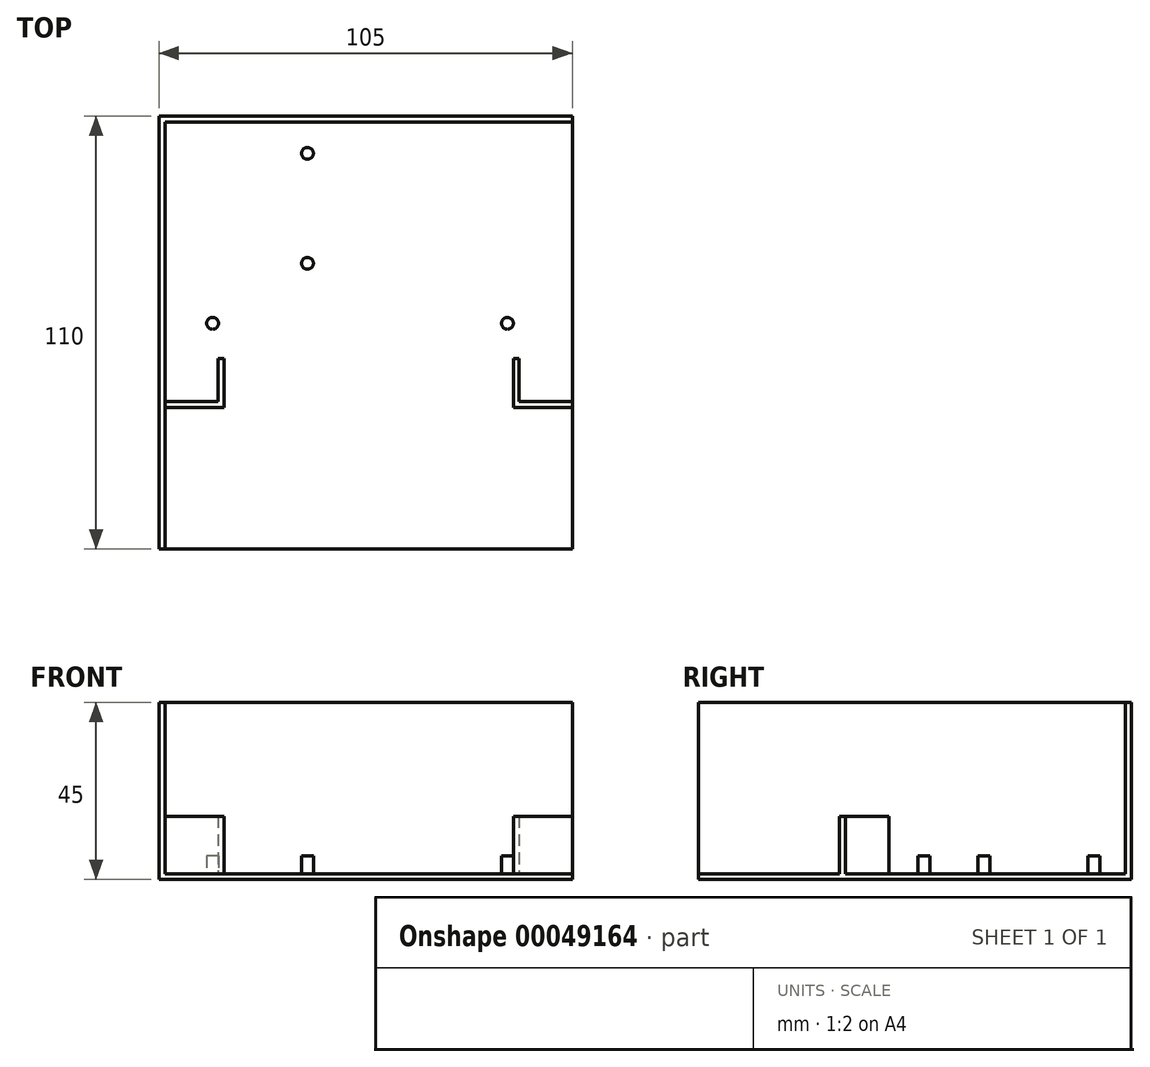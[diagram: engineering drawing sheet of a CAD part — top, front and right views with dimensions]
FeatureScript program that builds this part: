
annotation { "Feature Type Name" : "Feature", "Feature Type Description" : "" }
export const myFeature = defineFeature(function(context is Context, id is Id, definition is map)
    precondition{}
    {
        {
            var Q0;
            Q0=qCreatedBy(makeId("Top.planeOp"),FACE);
            var sketch = newSketch(context, id + "F0", { "sketchPlane" : qUnion([Q0])});
            skLineSegment(sketch, "E0.rect.bottom", {"start": v(52.5, 55) * mm, "end": v(-52.5, 55) * mm});
            skLineSegment(sketch, "E0.rect.top", {"start": v(52.5, -55) * mm, "end": v(-52.5, -55) * mm});
            skLineSegment(sketch, "E0.rect.left", {"start": v(52.5, 55) * mm, "end": v(52.5, -55) * mm});
            skLineSegment(sketch, "E0.rect.right", {"start": v(-52.5, 55) * mm, "end": v(-52.5, -55) * mm});
            skPoint(sketch, "E0.rect.middle", {"position": v(0, 0) * mm});
            skSolve(sketch);
        }
        {
            var Q0;
            Q0=makeQuery(id+"F0.imprint","IMPRINT",FACE,{"disambiguationData":[TD([[makeQuery(id+"F0.imprint","IMPRINT",EDGE,{"derivedFrom":sQuery(id+"F0.wireOp",EDGE,"E0.rect.bottom")}),1.0]])]});
            extrude(context, id + "F1", {"entities" : qUnion([Q0]), "depth" : 1.5 * mm});
        }
        {
            var Q0;
            Q0=makeQuery(id+"F1.opExtrude","CAP_FACE",FACE,{"disambiguationData":[OSD([sQuery(id+"F0.wireOp",EDGE,"E0.rect.bottom"),sQuery(id+"F0.wireOp",EDGE,"E0.rect.top"),sQuery(id+"F0.wireOp",EDGE,"E0.rect.left"),sQuery(id+"F0.wireOp",EDGE,"E0.rect.right")])],"isStart":false});
            var sketch = newSketch(context, id + "F2", { "sketchPlane" : qUnion([Q0])});
            skLineSegment(sketch, "E1.bottom", {"start": v(-52.5, 55) * mm, "end": v(52.5, 55) * mm});
            skLineSegment(sketch, "E1.top", {"start": v(-52.5, 53.5) * mm, "end": v(52.5, 53.5) * mm});
            skLineSegment(sketch, "E1.left", {"start": v(-52.5, 55) * mm, "end": v(-52.5, 53.5) * mm});
            skLineSegment(sketch, "E1.right", {"start": v(52.5, 55) * mm, "end": v(52.5, 53.5) * mm});
            skSolve(sketch);
        }
        {
            var Q0;
            Q0=makeQuery(id+"F2.imprint","IMPRINT",FACE,{"disambiguationData":[TD([[makeQuery(id+"F2.imprint","IMPRINT",EDGE,{"derivedFrom":sQuery(id+"F2.wireOp",EDGE,"E1.bottom")}),1.0]])]});
            extrude(context, id + "F3", {"entities" : qUnion([Q0]), "operationType" : NewBodyOperationType.ADD, "depth" : 43.5 * mm});
        }
        {
            var Q0;
            Q0=makeQuery(id+"F1.opExtrude","CAP_FACE",FACE,{"disambiguationData":[OSD([sQuery(id+"F0.wireOp",EDGE,"E0.rect.bottom"),sQuery(id+"F0.wireOp",EDGE,"E0.rect.top"),sQuery(id+"F0.wireOp",EDGE,"E0.rect.left"),sQuery(id+"F0.wireOp",EDGE,"E0.rect.right")])],"isStart":false});
            var sketch = newSketch(context, id + "F4", { "sketchPlane" : qUnion([Q0])});
            skLineSegment(sketch, "E2.bottom", {"start": v(-52.5, -55) * mm, "end": v(-51, -55) * mm});
            skLineSegment(sketch, "E2.top", {"start": v(-52.5, 53.5) * mm, "end": v(-51, 53.5) * mm});
            skLineSegment(sketch, "E2.left", {"start": v(-52.5, -55) * mm, "end": v(-52.5, 53.5) * mm});
            skLineSegment(sketch, "E2.right", {"start": v(-51, -55) * mm, "end": v(-51, 53.5) * mm});
            skSolve(sketch);
        }
        {
            var Q0;
            Q0=makeQuery(id+"F4.imprint","IMPRINT",FACE,{"disambiguationData":[TD([[makeQuery(id+"F4.imprint","IMPRINT",EDGE,{"derivedFrom":sQuery(id+"F4.wireOp",EDGE,"E2.bottom")}),-1.0]])]});
            extrude(context, id + "F5", {"entities" : qUnion([Q0]), "operationType" : NewBodyOperationType.ADD, "depth" : 43.5 * mm});
        }
        {
            var Q0;
            Q0=makeQuery(id+"F1.opExtrude","CAP_FACE",FACE,{"disambiguationData":[OSD([sQuery(id+"F0.wireOp",EDGE,"E0.rect.bottom"),sQuery(id+"F0.wireOp",EDGE,"E0.rect.top"),sQuery(id+"F0.wireOp",EDGE,"E0.rect.left"),sQuery(id+"F0.wireOp",EDGE,"E0.rect.right")])],"isStart":false});
            var sketch = newSketch(context, id + "F6", { "sketchPlane" : qUnion([Q0])});
            skCircle(sketch, "E3", {"center": v(-14.8, 45.5) * mm, "radius": 1.5 * mm});
            skCircle(sketch, "E4", {"center": v(-14.8, 17.56) * mm, "radius": 1.5 * mm});
            skCircle(sketch, "E5", {"center": v(-38.9, 2.3) * mm, "radius": 1.5 * mm});
            skCircle(sketch, "E6", {"center": v(36, 2.3) * mm, "radius": 1.5 * mm});
            skSolve(sketch);
        }
        {
            var Q0;
            Q0 = qSketchRegion(id + "F6", true);
            extrude(context, id + "F7", {"entities" : qUnion([Q0]), "operationType" : NewBodyOperationType.ADD, "depth" : 4.5 * mm});
        }
        {
            var Q0;
            Q0=makeQuery(id+"F1.opExtrude","CAP_FACE",FACE,{"disambiguationData":[OSD([sQuery(id+"F0.wireOp",EDGE,"E0.rect.bottom"),sQuery(id+"F0.wireOp",EDGE,"E0.rect.top"),sQuery(id+"F0.wireOp",EDGE,"E0.rect.left"),sQuery(id+"F0.wireOp",EDGE,"E0.rect.right")])],"isStart":false});
            var sketch = newSketch(context, id + "F8", { "sketchPlane" : qUnion([Q0])});
            skLineSegment(sketch, "E7.bottom", {"start": v(-51, -17.6) * mm, "end": v(-36, -17.6) * mm});
            skLineSegment(sketch, "E7.top", {"start": v(-51, -19.1) * mm, "end": v(-36, -19.1) * mm});
            skLineSegment(sketch, "E7.left", {"start": v(-51, -17.6) * mm, "end": v(-51, -19.1) * mm});
            skLineSegment(sketch, "E7.right", {"start": v(-36, -17.6) * mm, "end": v(-36, -19.1) * mm});
            skLineSegment(sketch, "E8.bottom", {"start": v(-36, -17.6) * mm, "end": v(-37.5, -17.6) * mm});
            skLineSegment(sketch, "E8.top", {"start": v(-36, -6.6) * mm, "end": v(-37.5, -6.6) * mm});
            skLineSegment(sketch, "E8.left", {"start": v(-36, -17.6) * mm, "end": v(-36, -6.6) * mm});
            skLineSegment(sketch, "E8.right", {"start": v(-37.5, -17.6) * mm, "end": v(-37.5, -6.6) * mm});
            skLineSegment(sketch, "E9.bottom", {"start": v(52.5, -19.1) * mm, "end": v(37.5, -19.1) * mm});
            skLineSegment(sketch, "E9.top", {"start": v(52.5, -17.6) * mm, "end": v(37.5, -17.6) * mm});
            skLineSegment(sketch, "E9.left", {"start": v(52.5, -19.1) * mm, "end": v(52.5, -17.6) * mm});
            skLineSegment(sketch, "E9.right", {"start": v(37.5, -19.1) * mm, "end": v(37.5, -17.6) * mm});
            skLineSegment(sketch, "E10.bottom", {"start": v(37.5, -17.6) * mm, "end": v(39, -17.6) * mm});
            skLineSegment(sketch, "E10.top", {"start": v(37.5, -6.6) * mm, "end": v(39, -6.6) * mm});
            skLineSegment(sketch, "E10.left", {"start": v(37.5, -17.6) * mm, "end": v(37.5, -6.6) * mm});
            skLineSegment(sketch, "E10.right", {"start": v(39, -17.6) * mm, "end": v(39, -6.6) * mm});
            skSolve(sketch);
        }
        {
            var Q0;
            Q0 = qSketchRegion(id + "F8", true);
            extrude(context, id + "F9", {"entities" : qUnion([Q0]), "operationType" : NewBodyOperationType.ADD, "depth" : 14.6 * mm});
        }
    });
